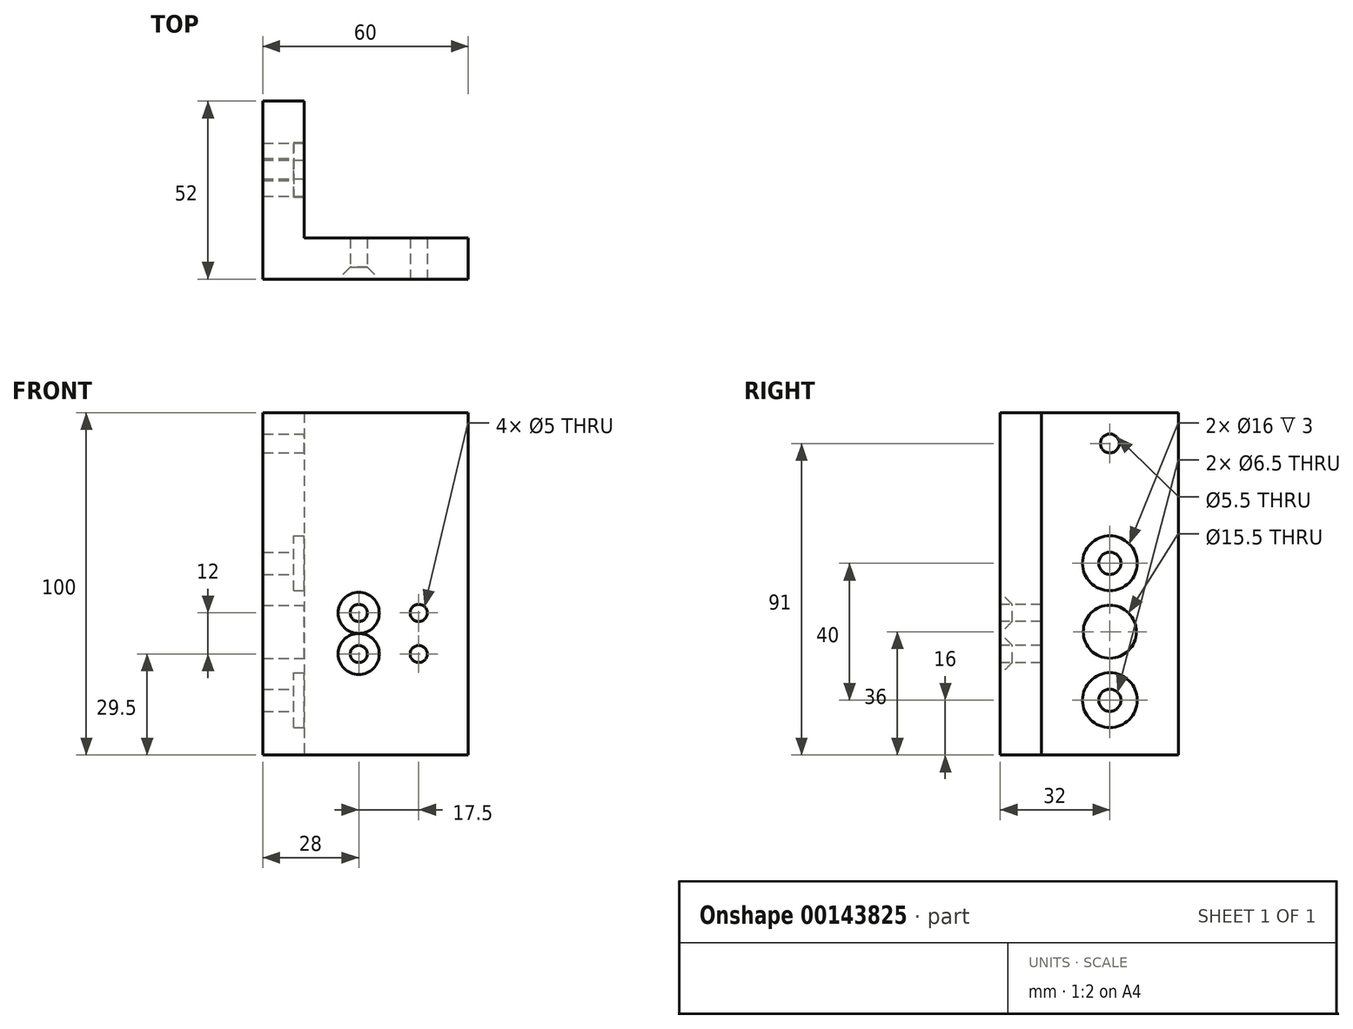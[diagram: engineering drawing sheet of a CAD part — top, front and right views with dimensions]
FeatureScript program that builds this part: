
annotation { "Feature Type Name" : "Feature", "Feature Type Description" : "" }
export const myFeature = defineFeature(function(context is Context, id is Id, definition is map)
    precondition{}
    {
        {
            var Q0;
            Q0=qCreatedBy(makeId("Front.planeOp"),FACE);
            var sketch = newSketch(context, id + "F0", { "sketchPlane" : qUnion([Q0])});
            skLineSegment(sketch, "E0.bottom", {"start": v(30, -50) * mm, "end": v(-30, -50) * mm});
            skLineSegment(sketch, "E0.top", {"start": v(30, 50) * mm, "end": v(-30, 50) * mm});
            skLineSegment(sketch, "E0.left", {"start": v(30, -50) * mm, "end": v(30, 50) * mm});
            skLineSegment(sketch, "E0.right", {"start": v(-30, -50) * mm, "end": v(-30, 50) * mm});
            skPoint(sketch, "E0.middle", {"position": v(0, 0) * mm});
            skSolve(sketch);
        }
        {
            var Q0;
            Q0=makeQuery(id+"F0.imprint","IMPRINT",FACE,{"disambiguationData":[TD([[makeQuery(id+"F0.imprint","IMPRINT",EDGE,{"derivedFrom":sQuery(id+"F0.wireOp",EDGE,"E0.bottom")}),-1.0]])]});
            extrude(context, id + "F1", {"entities" : qUnion([Q0]), "depth" : 10 * mm});
        }
        {
            var Q0;
            Q0=makeQuery(id+"F1.opExtrude","CAP_FACE",FACE,{"disambiguationData":[OSD([sQuery(id+"F0.wireOp",EDGE,"E0.bottom"),sQuery(id+"F0.wireOp",EDGE,"E0.top"),sQuery(id+"F0.wireOp",EDGE,"E0.left"),sQuery(id+"F0.wireOp",EDGE,"E0.right")])],"isStart":false});
            var sketch = newSketch(context, id + "F2", { "sketchPlane" : qUnion([Q0])});
            skLineSegment(sketch, "E1", {"start": v(-18, 50) * mm, "end": v(-18, -50) * mm});
            skSolve(sketch);
        }
        {
            var Q0;
            {var subQ0=sQuery(id+"F2.wireOp",EDGE,"E1");Q0=makeQuery(id+"F2.imprint","IMPRINT",FACE,{"disambiguationData":[TD([[makeQuery(id+"F2.imprint","IMPRINT",EDGE,{"derivedFrom":subQ0}),-1.0]])]});}
            extrude(context, id + "F3", {"entities" : qUnion([Q0]), "operationType" : NewBodyOperationType.ADD, "depth" : 40 * mm});
        }
        {
            var Q0;
            Q0=makeQuery(id+"F1.opExtrude","SWEPT_BODY",BODY,{"disambiguationData":[OSD([sQuery(id+"F0.wireOp",EDGE,"E0.bottom"),sQuery(id+"F0.wireOp",EDGE,"E0.top"),sQuery(id+"F0.wireOp",EDGE,"E0.left"),sQuery(id+"F0.wireOp",EDGE,"E0.right")])]});
            deleteBodies(context, id + "F4", {"entities" : qUnion([Q0])});
        }
        {
            var Q0;
            Q0=qCreatedBy(makeId("Front.planeOp"),FACE);
            var sketch = newSketch(context, id + "F5", { "sketchPlane" : qUnion([Q0])});
            skLineSegment(sketch, "E2.bottom", {"start": v(30, -50) * mm, "end": v(-30, -50) * mm});
            skLineSegment(sketch, "E2.top", {"start": v(30, 50) * mm, "end": v(-30, 50) * mm});
            skLineSegment(sketch, "E2.left", {"start": v(30, -50) * mm, "end": v(30, 50) * mm});
            skLineSegment(sketch, "E2.right", {"start": v(-30, -50) * mm, "end": v(-30, 50) * mm});
            skPoint(sketch, "E2.middle", {"position": v(0, 0) * mm});
            skSolve(sketch);
        }
        {
            var Q0;
            Q0=makeQuery(id+"F5.imprint","IMPRINT",FACE,{"disambiguationData":[TD([[makeQuery(id+"F5.imprint","IMPRINT",EDGE,{"derivedFrom":sQuery(id+"F5.wireOp",EDGE,"E2.bottom")}),-1.0]])]});
            extrude(context, id + "F6", {"entities" : qUnion([Q0]), "depth" : 12 * mm});
        }
        {
            var Q0;
            Q0=makeQuery(id+"F6.opExtrude","CAP_FACE",FACE,{"disambiguationData":[OSD([sQuery(id+"F5.wireOp",EDGE,"E2.bottom"),sQuery(id+"F5.wireOp",EDGE,"E2.top"),sQuery(id+"F5.wireOp",EDGE,"E2.left"),sQuery(id+"F5.wireOp",EDGE,"E2.right")])],"isStart":true});
            var sketch = newSketch(context, id + "F7", { "sketchPlane" : qUnion([Q0])});
            skLineSegment(sketch, "E3", {"start": v(18, 50) * mm, "end": v(18, -50) * mm});
            skSolve(sketch);
        }
        {
            var Q0;
            {var subQ0=sQuery(id+"F7.wireOp",EDGE,"E3");Q0=makeQuery(id+"F7.imprint","IMPRINT",FACE,{"disambiguationData":[TD([[makeQuery(id+"F7.imprint","IMPRINT",EDGE,{"derivedFrom":subQ0}),1.0]])]});}
            extrude(context, id + "F8", {"entities" : qUnion([Q0]), "operationType" : NewBodyOperationType.ADD, "depth" : 40 * mm});
        }
        {
            var Q0;
            Q0=makeQuery(id+"F6.opExtrude","CAP_FACE",FACE,{"disambiguationData":[OSD([sQuery(id+"F5.wireOp",EDGE,"E2.bottom"),sQuery(id+"F5.wireOp",EDGE,"E2.top"),sQuery(id+"F5.wireOp",EDGE,"E2.left"),sQuery(id+"F5.wireOp",EDGE,"E2.right")])],"isStart":false});
            var sketch = newSketch(context, id + "F9", { "sketchPlane" : qUnion([Q0])});
            skCircle(sketch, "E4", {"center": v(-2, -8.5) * mm, "radius": 3.03 * mm});
            skCircle(sketch, "E5", {"center": v(-2, -20.5) * mm, "radius": 3.16 * mm});
            skSolve(sketch);
        }
        {
            var Q0;
            Q0=sQuery(id+"F9.wireOp",VERTEX,"E4.center");
            var Q1;
            Q1=sQuery(id+"F9.wireOp",VERTEX,"E5.center");
            var Q2;
            Q2=makeQuery(id+"F6.opExtrude","SWEPT_BODY",BODY,{"disambiguationData":[OSD([sQuery(id+"F5.wireOp",EDGE,"E2.bottom"),sQuery(id+"F5.wireOp",EDGE,"E2.top"),sQuery(id+"F5.wireOp",EDGE,"E2.left"),sQuery(id+"F5.wireOp",EDGE,"E2.right")])]});
            hole(context, id + "F10", {"style" : HoleStyle.C_SINK, "endStyle" : HoleEndStyle.THROUGH, "standardTappedOrClearance" : lookupTablePath({ "standard" : "ISO", "size" : "5", "type" : "Drilled" }), "standardBlindInLast" : lookupTablePath({ "standard" : "ISO", "size" : "5", "type" : "Drilled" }), "holeDiameter" : 5 * mm, "cSinkDiameter" : 12 * mm, "cSinkAngle" : 90 * degree, "startFromSketch" : true, "locations" : qUnion([Q0, Q1]), "scope" : qUnion([Q2]), "isTappedThrough" : true});
        }
        {
            var Q0;
            Q0=makeQuery(id+"F6.opExtrude","CAP_FACE",FACE,{"disambiguationData":[OSD([sQuery(id+"F5.wireOp",EDGE,"E2.bottom"),sQuery(id+"F5.wireOp",EDGE,"E2.top"),sQuery(id+"F5.wireOp",EDGE,"E2.left"),sQuery(id+"F5.wireOp",EDGE,"E2.right")])],"isStart":false});
            var sketch = newSketch(context, id + "F11", { "sketchPlane" : qUnion([Q0])});
            skCircle(sketch, "E6", {"center": v(15.5, -8.5) * mm, "radius": 2.95 * mm});
            skCircle(sketch, "E7", {"center": v(15.5, -20.5) * mm, "radius": 3.08 * mm});
            skSolve(sketch);
        }
        {
            var Q0;
            Q0=sQuery(id+"F11.wireOp",VERTEX,"E6.center");
            var Q1;
            Q1=sQuery(id+"F11.wireOp",VERTEX,"E7.center");
            var Q2;
            Q2=makeQuery(id+"F6.opExtrude","SWEPT_BODY",BODY,{"disambiguationData":[OSD([sQuery(id+"F5.wireOp",EDGE,"E2.bottom"),sQuery(id+"F5.wireOp",EDGE,"E2.top"),sQuery(id+"F5.wireOp",EDGE,"E2.left"),sQuery(id+"F5.wireOp",EDGE,"E2.right")])]});
            hole(context, id + "F12", {"style" : HoleStyle.SIMPLE, "endStyle" : HoleEndStyle.THROUGH, "holeDiameter" : 5 * mm, "startFromSketch" : true, "locations" : qUnion([Q0, Q1]), "scope" : qUnion([Q2]), "isTappedThrough" : true});
        }
        {
            var Q0;
            Q0=makeQuery(id+"F8.opExtrude","SWEPT_FACE",FACE,{"disambiguationData":[OSD([sQuery(id+"F7.wireOp",EDGE,"E3")])]});
            var sketch = newSketch(context, id + "F13", { "sketchPlane" : qUnion([Q0])});
            skCircle(sketch, "E8", {"center": v(20, 6) * mm, "radius": 8 * mm});
            skCircle(sketch, "E9", {"center": v(20, -34) * mm, "radius": 8 * mm});
            skSolve(sketch);
        }
        {
            var Q0;
            Q0=makeQuery(id+"F13.imprint","IMPRINT",FACE,{"disambiguationData":[TD([[makeQuery(id+"F13.imprint","IMPRINT",EDGE,{"derivedFrom":sQuery(id+"F13.wireOp",EDGE,"E8")}),1.0]])]});
            var Q1;
            Q1=makeQuery(id+"F13.imprint","IMPRINT",FACE,{"disambiguationData":[TD([[makeQuery(id+"F13.imprint","IMPRINT",EDGE,{"derivedFrom":sQuery(id+"F13.wireOp",EDGE,"E9")}),1.0]])]});
            extrude(context, id + "F14", {"entities" : qUnion([Q0, Q1]), "operationType" : NewBodyOperationType.REMOVE, "oppositeDirection" : true, "depth" : 3 * mm});
        }
        {
            var Q0;
            Q0=makeQuery(id+"F14.boolean.opBoolean","COPY",FACE,{"derivedFrom":makeQuery(id+"F14.opExtrude","CAP_FACE",FACE,{"disambiguationData":[OSD([sQuery(id+"F13.wireOp",EDGE,"E8")])],"isStart":false})});
            var sketch = newSketch(context, id + "F15", { "sketchPlane" : qUnion([Q0])});
            skCircle(sketch, "E10", {"center": v(20, 6) * mm, "radius": 3.25 * mm});
            skSolve(sketch);
        }
        {
            var Q0;
            Q0=sQuery(id+"F15.wireOp",VERTEX,"E10.center");
            var Q1;
            Q1=makeQuery(id+"F6.opExtrude","SWEPT_BODY",BODY,{"disambiguationData":[OSD([sQuery(id+"F5.wireOp",EDGE,"E2.bottom"),sQuery(id+"F5.wireOp",EDGE,"E2.top"),sQuery(id+"F5.wireOp",EDGE,"E2.left"),sQuery(id+"F5.wireOp",EDGE,"E2.right")])]});
            hole(context, id + "F16", {"style" : HoleStyle.SIMPLE, "endStyle" : HoleEndStyle.THROUGH, "holeDiameter" : 6.5 * mm, "startFromSketch" : true, "locations" : qUnion([Q0]), "scope" : qUnion([Q1]), "isTappedThrough" : true});
        }
        {
            var Q0;
            Q0=makeQuery(id+"F14.boolean.opBoolean","COPY",FACE,{"derivedFrom":makeQuery(id+"F14.opExtrude","CAP_FACE",FACE,{"disambiguationData":[OSD([sQuery(id+"F13.wireOp",EDGE,"E9")])],"isStart":false})});
            var sketch = newSketch(context, id + "F17", { "sketchPlane" : qUnion([Q0])});
            skCircle(sketch, "E11", {"center": v(20, -34) * mm, "radius": 3.25 * mm});
            skSolve(sketch);
        }
        {
            var Q0;
            Q0=sQuery(id+"F17.wireOp",VERTEX,"E11.center");
            var Q1;
            Q1=makeQuery(id+"F6.opExtrude","SWEPT_BODY",BODY,{"disambiguationData":[OSD([sQuery(id+"F5.wireOp",EDGE,"E2.bottom"),sQuery(id+"F5.wireOp",EDGE,"E2.top"),sQuery(id+"F5.wireOp",EDGE,"E2.left"),sQuery(id+"F5.wireOp",EDGE,"E2.right")])]});
            hole(context, id + "F18", {"style" : HoleStyle.SIMPLE, "endStyle" : HoleEndStyle.THROUGH, "holeDiameter" : 6.5 * mm, "startFromSketch" : true, "locations" : qUnion([Q0]), "scope" : qUnion([Q1]), "isTappedThrough" : true});
        }
        {
            var Q0;
            Q0=makeQuery(id+"F8.opExtrude","SWEPT_FACE",FACE,{"disambiguationData":[OSD([sQuery(id+"F7.wireOp",EDGE,"E3")])]});
            var sketch = newSketch(context, id + "F19", { "sketchPlane" : qUnion([Q0])});
            skCircle(sketch, "E12", {"center": v(20, 41) * mm, "radius": 2.1 * mm});
            skSolve(sketch);
        }
        {
            var Q0;
            Q0=sQuery(id+"F19.wireOp",VERTEX,"E12.center");
            var Q1;
            Q1=makeQuery(id+"F6.opExtrude","SWEPT_BODY",BODY,{"disambiguationData":[OSD([sQuery(id+"F5.wireOp",EDGE,"E2.bottom"),sQuery(id+"F5.wireOp",EDGE,"E2.top"),sQuery(id+"F5.wireOp",EDGE,"E2.left"),sQuery(id+"F5.wireOp",EDGE,"E2.right")])]});
            hole(context, id + "F20", {"style" : HoleStyle.SIMPLE, "endStyle" : HoleEndStyle.THROUGH, "standardTappedOrClearance" : lookupTablePath({ "standard" : "ISO", "fit" : "Normal", "size" : "M5", "type" : "Clearance" }), "standardBlindInLast" : lookupTablePath({ "fit" : "Standard", "standard" : "ISO", "size" : "M5", "type" : "Clearance" }), "holeDiameter" : 5.5 * mm, "startFromSketch" : true, "locations" : qUnion([Q0]), "scope" : qUnion([Q1]), "isTappedThrough" : true});
        }
        {
            var Q0;
            Q0=makeQuery(id+"F8.opExtrude","SWEPT_FACE",FACE,{"disambiguationData":[OSD([sQuery(id+"F7.wireOp",EDGE,"E3")])]});
            var sketch = newSketch(context, id + "F21", { "sketchPlane" : qUnion([Q0])});
            skCircle(sketch, "E13", {"center": v(20, -14) * mm, "radius": 6.5 * mm});
            skSolve(sketch);
        }
        {
            var Q0;
            Q0=sQuery(id+"F21.wireOp",VERTEX,"E13.center");
            var Q1;
            Q1=makeQuery(id+"F6.opExtrude","SWEPT_BODY",BODY,{"disambiguationData":[OSD([sQuery(id+"F5.wireOp",EDGE,"E2.bottom"),sQuery(id+"F5.wireOp",EDGE,"E2.top"),sQuery(id+"F5.wireOp",EDGE,"E2.left"),sQuery(id+"F5.wireOp",EDGE,"E2.right")])]});
            hole(context, id + "F22", {"style" : HoleStyle.SIMPLE, "endStyle" : HoleEndStyle.THROUGH, "standardTappedOrClearance" : lookupTablePath({ "standard" : "ISO", "fit" : "Normal", "size" : "M14", "type" : "Clearance" }), "standardBlindInLast" : lookupTablePath({ "fit" : "Standard", "standard" : "ISO", "size" : "M14", "type" : "Clearance" }), "holeDiameter" : 15.5 * mm, "startFromSketch" : true, "locations" : qUnion([Q0]), "scope" : qUnion([Q1]), "isTappedThrough" : true});
        }
    });
